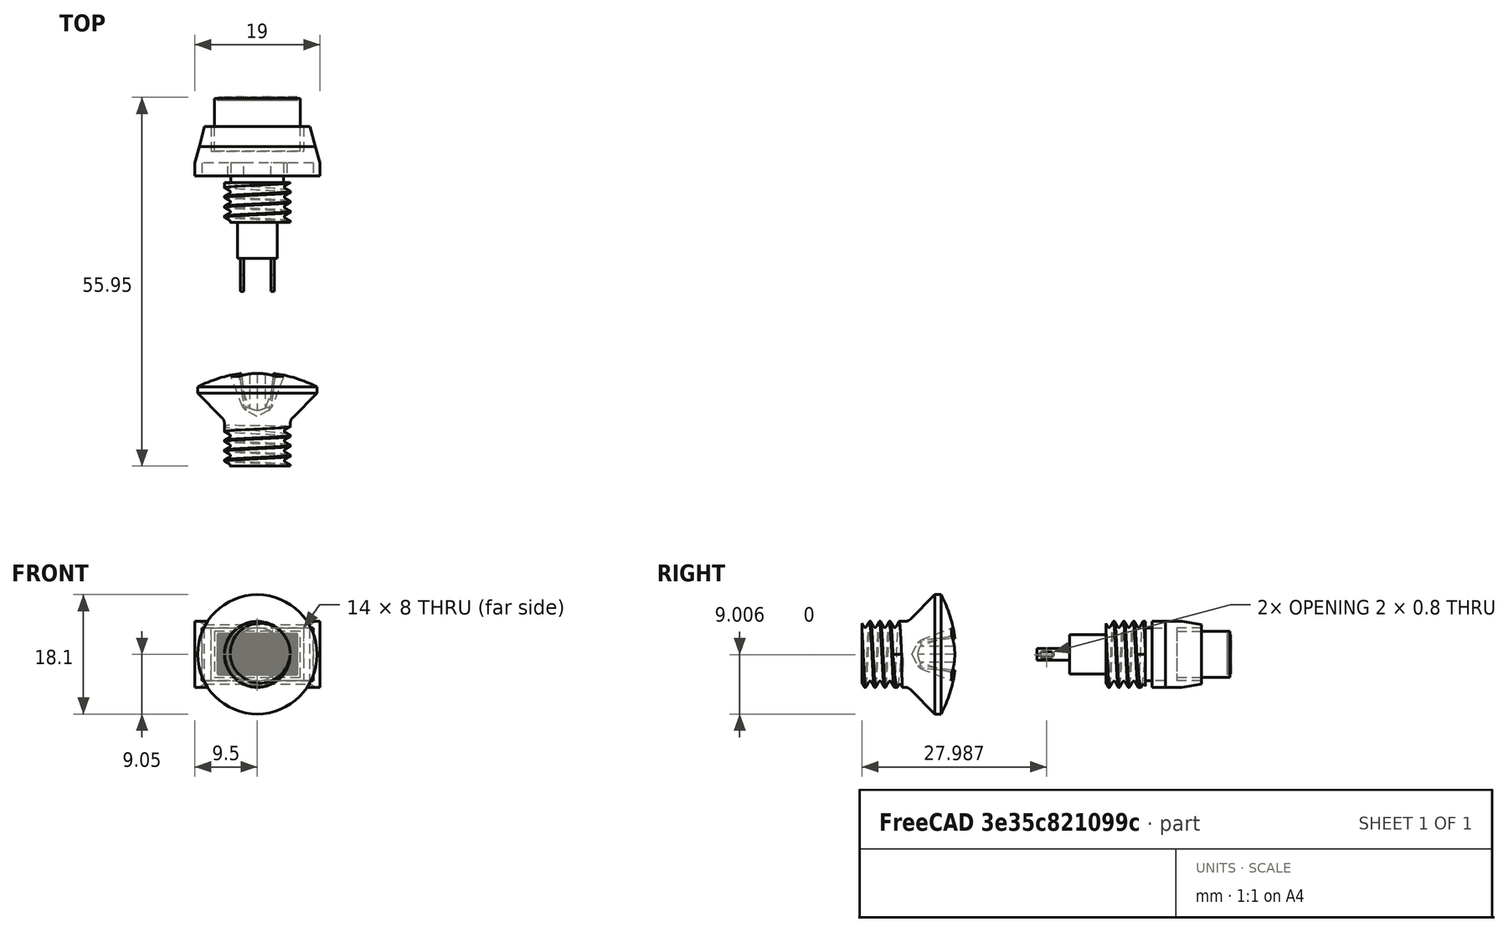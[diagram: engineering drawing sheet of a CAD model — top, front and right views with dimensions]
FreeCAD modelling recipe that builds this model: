
FCSTD DOCUMENT  (FreeCAD 0.18R16110 (Git))
Label: Miyama DS-462 4
License: All rights reserved
LicenseURL: http://en.wikipedia.org/wiki/All_rights_reserved
objects: Sketcher::SketchObject×13, Part::Extrusion×10, Part::Cut×4, Part::MultiFuse×3, Part::FeaturePython×2, Part::Feature×2, Part::Cone×1, Part::Sweep×1, Part::MultiCommon×1, Part::Box×1
note: 38 computed .brp shape members not serialized (recipe doc carries the construction recipe); baked Part::Feature solids carry a one-line shape summary decoded from their .brp

FEATURE [Sketcher::SketchObject] Sketch
  sketch-geometry (12):
    g0: LineSegment [constr] StartX=-7 StartY=11.8 StartZ=0 EndX=7 EndY=11.8 EndZ=0
    g1: LineSegment [constr] StartX=-9.5 StartY=0 StartZ=0 EndX=9.5 EndY=0 EndZ=0
    g2: LineSegment [constr] StartX=-7 StartY=11.8 StartZ=0 EndX=-7 EndY=7.5 EndZ=0
    g3: LineSegment [constr] StartX=7 StartY=7.5 StartZ=0 EndX=7 EndY=11.8 EndZ=0
    g4: LineSegment [constr] StartX=9.5 StartY=0 StartZ=0 EndX=9.5 EndY=2 EndZ=0
    g5: LineSegment [constr] StartX=9.5 StartY=2 StartZ=0 EndX=7 EndY=7.5 EndZ=0
    g6: LineSegment [constr] StartX=-9.5 StartY=0 StartZ=0 EndX=-9.5 EndY=2 EndZ=0
    g7: LineSegment [constr] StartX=-9.5 StartY=2 StartZ=0 EndX=-7 EndY=7.5 EndZ=0
    g8: LineSegment StartX=-9.5 StartY=2 StartZ=0 EndX=-9.5 EndY=0 EndZ=0
    g9: LineSegment StartX=-9.5 StartY=0 StartZ=0 EndX=9.5 EndY=0 EndZ=0
    g10: LineSegment StartX=9.5 StartY=0 StartZ=0 EndX=9.5 EndY=2 EndZ=0
    g11: LineSegment StartX=9.5 StartY=2 StartZ=0 EndX=-9.5 EndY=2 EndZ=0
  constraints (31):
    c: DistanceX(g0,g0) = 14
    c: DistanceX(g1,g1) = 19
    c: Symmetric(g0,g0,g-2)
    c: Coincident(g2,g0)
    c: Vertical(g2)
    c: Coincident(g3,g0)
    c: Vertical(g3)
    c: DistanceY(g3,g3) = 4.3
    c: Coincident(g4,g1)
    c: Coincident(g5,g4)
    c: Coincident(g7,g6)
    c: Coincident(g7,g2)
    c: Vertical(g6)
    c: Vertical(g4)
    c: DistanceY(g1,g5) = 7.5
    c: Equal(g4,g6)
    c: Coincident(g6,g1)
    c: DistanceY(g4,g4) = 2
    c: PointOnObject(g-1,g1)
    c: Horizontal(g1)
    c: Equal(g7,g5)
    c: Coincident(g3,g5)
    c: Equal(g3,g2)
    c: Coincident(g6,g8)
    c: Coincident(g8,g1)
    c: Coincident(g8,g9)
    c: Coincident(g9,g1)
    c: Coincident(g9,g10)
    c: Coincident(g10,g4)
    c: Coincident(g10,g11)
    c: Coincident(g11,g8)
FEATURE [Sketcher::SketchObject] Sketch001
  sketch-geometry (12):
    g0: LineSegment [constr] StartX=-8 StartY=11.8 StartZ=0 EndX=8 EndY=11.8 EndZ=0
    g1: LineSegment [constr] StartX=-9.5 StartY=0 StartZ=0 EndX=9.5 EndY=0 EndZ=0
    g2: LineSegment [constr] StartX=-8 StartY=11.8 StartZ=0 EndX=-8 EndY=7.5 EndZ=0
    g3: LineSegment [constr] StartX=8 StartY=7.5 StartZ=0 EndX=8 EndY=11.8 EndZ=0
    g4: LineSegment [constr] StartX=9.5 StartY=0 StartZ=0 EndX=9.5 EndY=2 EndZ=0
    g5: LineSegment [constr] StartX=9.5 StartY=2 StartZ=0 EndX=8 EndY=7.5 EndZ=0
    g6: LineSegment [constr] StartX=-9.5 StartY=0 StartZ=0 EndX=-9.5 EndY=2 EndZ=0
    g7: LineSegment [constr] StartX=-9.5 StartY=2 StartZ=0 EndX=-8 EndY=7.5 EndZ=0
    g8: LineSegment StartX=-9.5 StartY=2 StartZ=0 EndX=-8 EndY=7.5 EndZ=0
    g9: LineSegment StartX=-8 StartY=7.5 StartZ=0 EndX=8 EndY=7.5 EndZ=0
    g10: LineSegment StartX=8 StartY=7.5 StartZ=0 EndX=9.5 EndY=2 EndZ=0
    g11: LineSegment StartX=9.5 StartY=2 StartZ=0 EndX=-9.5 EndY=2 EndZ=0
  constraints (31):
    c: DistanceX(g0,g0) = 16
    c: DistanceX(g1,g1) = 19
    c: Symmetric(g0,g0,g-2)
    c: Coincident(g2,g0)
    c: Vertical(g2)
    c: Coincident(g3,g0)
    c: Vertical(g3)
    c: DistanceY(g3,g3) = 4.3
    c: Coincident(g4,g1)
    c: Coincident(g5,g4)
    c: Coincident(g7,g6)
    c: Coincident(g7,g2)
    c: Vertical(g6)
    c: Vertical(g4)
    c: DistanceY(g1,g5) = 7.5
    c: Equal(g4,g6)
    c: Coincident(g6,g1)
    c: DistanceY(g4,g4) = 2
    c: PointOnObject(g-1,g1)
    c: Horizontal(g1)
    c: Equal(g7,g5)
    c: Coincident(g3,g5)
    c: Equal(g3,g2)
    c: Coincident(g6,g8)
    c: Coincident(g8,g2)
    c: Coincident(g8,g9)
    c: Coincident(g9,g10)
    c: Coincident(g10,g4)
    c: Coincident(g10,g11)
    c: Coincident(g11,g8)
    c: Coincident(g9,g3)
FEATURE [Sketcher::SketchObject] Sketch002
  sketch-geometry (12):
    g0: LineSegment [constr] StartX=-7 StartY=11.8 StartZ=0 EndX=7 EndY=11.8 EndZ=0
    g1: LineSegment [constr] StartX=-9.5 StartY=0 StartZ=0 EndX=9.5 EndY=0 EndZ=0
    g2: LineSegment [constr] StartX=-7 StartY=11.8 StartZ=0 EndX=-7 EndY=7.5 EndZ=0
    g3: LineSegment [constr] StartX=7 StartY=7.5 StartZ=0 EndX=7 EndY=11.8 EndZ=0
    g4: LineSegment [constr] StartX=9.5 StartY=0 StartZ=0 EndX=9.5 EndY=2 EndZ=0
    g5: LineSegment [constr] StartX=9.5 StartY=2 StartZ=0 EndX=7 EndY=7.5 EndZ=0
    g6: LineSegment [constr] StartX=-9.5 StartY=0 StartZ=0 EndX=-9.5 EndY=2 EndZ=0
    g7: LineSegment [constr] StartX=-9.5 StartY=2 StartZ=0 EndX=-7 EndY=7.5 EndZ=0
    g8: LineSegment StartX=-7 StartY=11.8 StartZ=0 EndX=-7 EndY=7.5 EndZ=0
    g9: LineSegment StartX=-7 StartY=7.5 StartZ=0 EndX=7 EndY=7.5 EndZ=0
    g10: LineSegment StartX=7 StartY=7.5 StartZ=0 EndX=7 EndY=11.8 EndZ=0
    g11: LineSegment StartX=7 StartY=11.8 StartZ=0 EndX=-7 EndY=11.8 EndZ=0
  constraints (31):
    c: DistanceX(g0,g0) = 14
    c: DistanceX(g1,g1) = 19
    c: Symmetric(g0,g0,g-2)
    c: Coincident(g2,g0)
    c: Vertical(g2)
    c: Coincident(g3,g0)
    c: Vertical(g3)
    c: DistanceY(g3,g3) = 4.3
    c: Coincident(g4,g1)
    c: Coincident(g5,g4)
    c: Coincident(g7,g6)
    c: Coincident(g7,g2)
    c: Vertical(g6)
    c: Vertical(g4)
    c: DistanceY(g1,g5) = 7.5
    c: Equal(g4,g6)
    c: Coincident(g6,g1)
    c: DistanceY(g4,g4) = 2
    c: PointOnObject(g-1,g1)
    c: Horizontal(g1)
    c: Equal(g7,g5)
    c: Coincident(g3,g5)
    c: Equal(g3,g2)
    c: Coincident(g0,g8)
    c: Coincident(g8,g2)
    c: Coincident(g8,g9)
    c: Coincident(g9,g3)
    c: Coincident(g9,g10)
    c: Coincident(g10,g0)
    c: Coincident(g10,g11)
    c: Coincident(g11,g8)
FEATURE [Part::Extrusion] Extrude
  Base = -> Sketch
  Dir = (0,0,1)
  DirMode = 2
  FaceMakerClass = Part::FaceMakerBullseye
  LengthFwd = 10
  LengthRev = 0
  Solid = true
  Symmetric = false
FEATURE [Part::Extrusion] Extrude001
  Base = -> Sketch001
  Dir = (0,0,1)
  DirMode = 2
  FaceMakerClass = Part::FaceMakerBullseye
  LengthFwd = 10
  LengthRev = 0
  Solid = true
  Symmetric = false
FEATURE [Sketcher::SketchObject] Sketch003
  MapMode = 5
  Placement = pos=(0,7.5,0) rot=(0,0.707107,0.707107;3.14159rad)
  Support = -> [Extrude001]
  sketch-geometry (4):
    g0: LineSegment StartX=-7 StartY=9 StartZ=0 EndX=-7 EndY=1 EndZ=0
    g1: LineSegment StartX=-7 StartY=1 StartZ=0 EndX=7 EndY=1 EndZ=0
    g2: LineSegment StartX=7 StartY=1 StartZ=0 EndX=7 EndY=9 EndZ=0
    g3: LineSegment StartX=7 StartY=9 StartZ=0 EndX=-7 EndY=9 EndZ=0
  constraints (8):
    c: Vertical(g0)
    c: Coincident(g0,g1)
    c: Horizontal(g1)
    c: Coincident(g1,g2)
    c: Vertical(g2)
    c: Coincident(g2,g3)
    c: Coincident(g3,g0)
    c: Horizontal(g3)
FEATURE [Part::Extrusion] Extrude002
  Base = -> Sketch003
  Dir = (0,1,-2e-16)
  DirMode = 2
  FaceMakerClass = Part::FaceMakerBullseye
  LengthFwd = -7.5
  LengthRev = 0
  Solid = true
  Symmetric = true
FEATURE [Part::Cut] Cut
  Base = -> Extrude001
  Tool = -> Extrude002
FEATURE [Sketcher::SketchObject] Sketch004
  MapMode = 5
  Placement = pos=(0,3.75,-8e-16) rot=(0,0.707107,0.707107;3.14159rad)
  Support = -> [Cut]
  sketch-geometry (4):
    g0: LineSegment StartX=-6.5 StartY=8.5 StartZ=0 EndX=6.5 EndY=8.5 EndZ=0
    g1: LineSegment StartX=6.5 StartY=8.5 StartZ=0 EndX=6.5 EndY=1.5 EndZ=0
    g2: LineSegment StartX=6.5 StartY=1.5 StartZ=0 EndX=-6.5 EndY=1.5 EndZ=0
    g3: LineSegment StartX=-6.5 StartY=1.5 StartZ=0 EndX=-6.5 EndY=8.5 EndZ=0
  constraints (8):
    c: Coincident(g0,g1)
    c: Coincident(g1,g2)
    c: Coincident(g2,g3)
    c: Coincident(g3,g0)
    c: Horizontal(g0)
    c: Horizontal(g2)
    c: Vertical(g1)
    c: Vertical(g3)
FEATURE [Part::Extrusion] Extrude003
  Base = -> Sketch004
  Dir = (0,1,-2e-16)
  DirMode = 2
  FaceMakerClass = Part::FaceMakerBullseye
  LengthFwd = 8.05
  LengthRev = 0
  Solid = true
  Symmetric = false
FEATURE [Part::Cone] Cone
  Angle = 360
  AttacherType = Attacher::AttachEngine3D
  Height = 0.5
  Placement = pos=(-5.85,11.45,7.9) rot=(-1,0,0;1.5708rad)
  Radius1 = 0.25
  Radius2 = 0.01
FEATURE [Part::FeaturePython] Array  # Draft array (typed FeaturePython)
  Angle = 360
  ArrayType = 0
  Axis = (0,0,1)
  Base = -> Cone
  Center = (0,0,0)
  Fuse = false
  IntervalAxis = (0,0,0)
  IntervalX = (0.25,0,0)
  IntervalY = (0,1,0)
  IntervalZ = (0,0,-0.25)
  NumberPolar = 1
  NumberX = 48
  NumberY = 1
  NumberZ = 24
FEATURE [Sketcher::SketchObject] Sketch005
  MapMode = 5
  Placement = pos=(0,0,0) rot=(1,0,0;1.5708rad)
  Support = -> [Extrude]
  sketch-geometry (4):
    g0: LineSegment StartX=-8.39842 StartY=9 StartZ=0 EndX=8.5 EndY=9 EndZ=0
    g1: LineSegment StartX=8.5 StartY=9 StartZ=0 EndX=8.5 EndY=1 EndZ=0
    g2: LineSegment StartX=8.5 StartY=1 StartZ=0 EndX=-8.39842 EndY=1 EndZ=0
    g3: LineSegment StartX=-8.39842 StartY=1 StartZ=0 EndX=-8.39842 EndY=9 EndZ=0
  constraints (8):
    c: Coincident(g0,g1)
    c: Coincident(g1,g2)
    c: Coincident(g2,g3)
    c: Coincident(g3,g0)
    c: Horizontal(g0)
    c: Horizontal(g2)
    c: Vertical(g1)
    c: Vertical(g3)
FEATURE [Part::Extrusion] Extrude004
  Base = -> Sketch005
  Dir = (0,-1,2e-16)
  DirMode = 2
  FaceMakerClass = Part::FaceMakerBullseye
  LengthFwd = 5
  LengthRev = 0
  Solid = true
  Symmetric = true
FEATURE [Part::Cut] Cut001
  Base = -> Extrude
  Tool = -> Extrude004
FEATURE [Sketcher::SketchObject] Sketch006
  MapMode = 5
  Placement = pos=(0,2,0) rot=(1,0,0;1.5708rad)
  Support = -> [Cut]
  sketch-geometry (1):
    g0: Circle CenterX=0 CenterY=5 CenterZ=0 NormalX=0 NormalY=0 NormalZ=1 AngleXU=0 Radius=4
  constraints (2):
    c: PointOnObject(g0,g-2)
    c: Radius(g0) = 4
FEATURE [Sketcher::SketchObject] Sketch007
  ExternalGeometry = -> [Cut]
  sketch-geometry (1):
    g0: LineSegment StartX=0 StartY=2 StartZ=0 EndX=0 EndY=-7 EndZ=0
  constraints (1):
    c: DistanceY(g0,g0) = 9
FEATURE [Part::Sweep] Sweep
  Frenet = false
  Sections = -> [Sketch006]
  Solid = true
  Spine = -> Sketch007
  Transition = 1
FEATURE [Sketcher::SketchObject] Sketch008
  MapMode = 5
  Placement = pos=(0,-7,0) rot=(1,0,0;1.5708rad)
  Support = -> [Sweep]
  sketch-geometry (1):
    g0: Circle CenterX=0 CenterY=5 CenterZ=0 NormalX=0 NormalY=0 NormalZ=1 AngleXU=0 Radius=3
  constraints (1):
    c: PointOnObject(g0,g-2)
FEATURE [Part::Extrusion] Extrude005
  Base = -> Sketch008
  Dir = (0,-1,2e-16)
  DirMode = 2
  FaceMakerClass = Part::FaceMakerBullseye
  LengthFwd = 5.5
  LengthRev = 0
  Solid = true
  Symmetric = false
FEATURE [Sketcher::SketchObject] Sketch009
  MapMode = 5
  Placement = pos=(-1.2e-15,-12.5,2.1e-15) rot=(1,0,0;1.5708rad)
  Support = -> [Extrude005]
  sketch-geometry (10):
    g0: LineSegment StartX=-2.55 StartY=5.89295 StartZ=0 EndX=-2.05 EndY=5.89295 EndZ=0
    g1: LineSegment StartX=-2.05 StartY=5.89295 StartZ=0 EndX=-2.05 EndY=4.09295 EndZ=0
    g2: LineSegment StartX=-2.05 StartY=4.09295 StartZ=0 EndX=-2.55 EndY=4.09295 EndZ=0
    g3: LineSegment StartX=-2.55 StartY=4.09295 StartZ=0 EndX=-2.55 EndY=5.89295 EndZ=0
    g4: LineSegment [constr] StartX=0 StartY=10 StartZ=0 EndX=0 EndY=0 EndZ=0
    g5: LineSegment [constr] StartX=-9.45869 StartY=4.99295 StartZ=0 EndX=9.50951 EndY=4.99295 EndZ=0
    g6: LineSegment StartX=2.55 StartY=5.89295 StartZ=0 EndX=2.55 EndY=4.09295 EndZ=0
    g7: LineSegment StartX=2.05 StartY=5.89295 StartZ=0 EndX=2.55 EndY=5.89295 EndZ=0
    g8: LineSegment StartX=2.05 StartY=4.09295 StartZ=0 EndX=2.05 EndY=5.89295 EndZ=0
    g9: LineSegment StartX=2.55 StartY=4.09295 StartZ=0 EndX=2.05 EndY=4.09295 EndZ=0
  constraints (27):
    c: Coincident(g0,g1)
    c: Coincident(g1,g2)
    c: Coincident(g2,g3)
    c: Coincident(g3,g0)
    c: Horizontal(g0)
    c: Horizontal(g2)
    c: Vertical(g1)
    c: Vertical(g3)
    c: DistanceX(g0,g0) = 0.5
    c: DistanceY(g1,g1) = 1.8
    c: PointOnObject(g4,g-2)
    c: Coincident(g4,g-1)
    c: Horizontal(g5)
    c: DistanceY(g5,g0) = 0.9
    c: DistanceX(g1,g-1) = 2.05
    c: Coincident(g7,g6)
    c: Coincident(g6,g9)
    c: Coincident(g9,g8)
    c: Coincident(g8,g7)
    c: Horizontal(g7)
    c: Horizontal(g9)
    c: Vertical(g6)
    c: Vertical(g8)
    c: DistanceX(g7,g7) = 0.5
    c: DistanceY(g6,g6) = 1.8
    c: DistanceX(g-1,g8) = 2.05
    c: DistanceY(g5,g7) = 0.9
FEATURE [Part::Extrusion] Extrude006
  Base = -> Sketch009
  Dir = (-1e-16,-1,2e-16)
  DirMode = 2
  FaceMakerClass = Part::FaceMakerBullseye
  LengthFwd = 5
  LengthRev = 0
  Solid = true
  Symmetric = false
FEATURE [Sketcher::SketchObject] Sketch010
  MapMode = 5
  Placement = pos=(2.55,-3e-16,0) rot=(0.57735,0.57735,0.57735;2.0944rad)
  Support = -> [Extrude006]
  sketch-geometry (9):
    g0: LineSegment StartX=-16.7272 StartY=5.35582 StartZ=0 EndX=-15.2992 EndY=5.35582 EndZ=0
    g1: LineSegment StartX=-15.0132 StartY=5.06984 StartZ=0 EndX=-15.0132 EndY=4.8418 EndZ=0
    g2: LineSegment StartX=-15.2992 StartY=4.55582 StartZ=0 EndX=-16.7272 EndY=4.55582 EndZ=0
    g3: LineSegment StartX=-17.0132 StartY=4.8418 StartZ=0 EndX=-17.0132 EndY=5.06984 EndZ=0
    g4: LineSegment [constr] StartX=-17.5132 StartY=4 StartZ=0 EndX=-17.5132 EndY=5 EndZ=0
    g5: ArcOfCircle CenterX=-15.2992 CenterY=5.06984 CenterZ=0 NormalX=0 NormalY=0 NormalZ=1 AngleXU=0 Radius=0.285978 StartAngle=1.3e-15 EndAngle=1.5708
    g6: ArcOfCircle CenterX=-16.7272 CenterY=5.06984 CenterZ=0 NormalX=0 NormalY=0 NormalZ=1 AngleXU=0 Radius=0.285978 StartAngle=1.5708 EndAngle=3.14159
    g7: ArcOfCircle CenterX=-15.2992 CenterY=4.8418 CenterZ=0 NormalX=0 NormalY=0 NormalZ=1 AngleXU=0 Radius=0.285978 StartAngle=4.71239 EndAngle=6.28319
    g8: ArcOfCircle CenterX=-16.7272 CenterY=4.8418 CenterZ=0 NormalX=0 NormalY=0 NormalZ=1 AngleXU=0 Radius=0.285978 StartAngle=3.14159 EndAngle=4.71239
  constraints (21):
    c: Horizontal(g0)
    c: Horizontal(g2)
    c: Vertical(g1)
    c: Vertical(g3)
    c: Vertical(g4)
    c: DistanceX(g4) = -17.5132
    c: DistanceY(g4) = 5
    c: Tangent(g1,g5) = 1.5708
    c: Tangent(g0,g5) = 1.5708
    c: Tangent(g0,g6) = 1.5708
    c: Tangent(g3,g6) = 1.5708
    c: Tangent(g1,g7) = 1.5708
    c: Tangent(g2,g7) = 1.5708
    c: Tangent(g2,g8) = 1.5708
    c: Tangent(g3,g8) = 1.5708
    c: DistanceX(g6,g8) = 0
    c: DistanceX(g5,g7) = 0
    c: DistanceX(g4,g3) = 0.5
    c: Equal(g6,g5)
    c: DistanceY(g2,g0) = 0.8
    c: DistanceX(g3,g1) = 2
FEATURE [Part::Extrusion] Extrude007
  Base = -> Sketch010
  Dir = (1,0,0)
  DirMode = 2
  FaceMakerClass = Part::FaceMakerBullseye
  LengthFwd = 20
  LengthRev = 0
  Reversed = true
  Solid = true
  Symmetric = true
FEATURE [Part::Cut] Cut002
  Base = -> Extrude006
  Tool = -> Extrude007
FEATURE [Sketcher::SketchObject] Sketch011
  MapMode = 5
  Placement = pos=(-9.5,0,0) rot=(0.57735,-0.57735,-0.57735;2.0944rad)
  Support = -> [Cut001]
  sketch-geometry (4):
    g0: LineSegment StartX=-1.5 StartY=10.5 StartZ=0 EndX=-7.5 EndY=9.5 EndZ=0
    g1: LineSegment StartX=-7.5 StartY=9.5 StartZ=0 EndX=-7.5 EndY=0.5 EndZ=0
    g2: LineSegment StartX=-7.5 StartY=0.5 StartZ=0 EndX=-1.5 EndY=-0.5 EndZ=0
    g3: LineSegment StartX=-1.5 StartY=-0.5 StartZ=0 EndX=-1.5 EndY=10.5 EndZ=0
  constraints (6):
    c: Coincident(g0,g1)
    c: Vertical(g1)
    c: Coincident(g1,g2)
    c: Coincident(g2,g3)
    c: Coincident(g3,g0)
    c: Vertical(g3)
FEATURE [Part::Extrusion] Extrude008
  Base = -> Sketch011
  Dir = (-1,0,0)
  DirMode = 2
  FaceMakerClass = Part::FaceMakerBullseye
  LengthFwd = 19
  LengthRev = 0
  Reversed = true
  Solid = true
  Symmetric = false
FEATURE [Part::MultiCommon] Common
  Shapes = -> [Cut,Extrude008]
FEATURE [Part::FeaturePython] Screw  label="M10x12-Screw"  # Fasteners workbench fastener (typed FeaturePython)
  Placement = pos=(0,-32,5) rot=(-1,0,0;1.5708rad)
  baseObject = -> Sweep [Edge3]
  diameter = 10
  invert = true
  length = 0
  matchOuter = false
  offset = -25
  thread = true
  type = 18
FEATURE [Part::Box] Box  label="Cube"
  AttacherType = Attacher::AttachEngine3D
  Height = 20
  Length = 30
  Placement = pos=(-12,-38,-5) rot=(0,0,1;0rad)
  Width = 15
FEATURE [Part::Feature] M10x12_Screw_Copy
  Placement = pos=(0,-32,5) rot=(-1,0,0;1.5708rad)
  shape: bbox 18.1 x 15.58 x 18.1 mm, 46 faces (baked)
FEATURE [Part::Cut] Cut003
  Base = -> M10x12_Screw_Copy
  Placement = pos=(0,37,0) rot=(0,0,1;0rad)
  Tool = -> Box
FEATURE [Part::MultiFuse] Fusion
  Shapes = -> [Sweep,Cut003]
FEATURE [Sketcher::SketchObject] Sketch012
  MapMode = 5
  Placement = pos=(0,2,0) rot=(1,0,0;1.5708rad)
  Support = -> [Common]
  sketch-geometry (1):
    g0: Circle CenterX=0 CenterY=5 CenterZ=0 NormalX=0 NormalY=0 NormalZ=1 AngleXU=0 Radius=4.5
  constraints (1):
    c: Radius(g0) = 4.5
FEATURE [Part::Extrusion] Extrude009
  Base = -> Sketch012
  Dir = (0,-1,2e-16)
  DirMode = 2
  FaceMakerClass = Part::FaceMakerBullseye
  LengthFwd = 2
  LengthRev = 0
  Solid = true
  Symmetric = false
FEATURE [Part::MultiFuse] Fusion001
  Shapes = -> [Common,Extrude009]
FEATURE [Part::MultiFuse] Fusion002
  Shapes = -> [Fusion001,Cut001]
FEATURE [Part::Feature] Fusion002001  label="Fusion003"
  shape: bbox 19 x 7.502 x 10 mm, 25 faces (baked)
